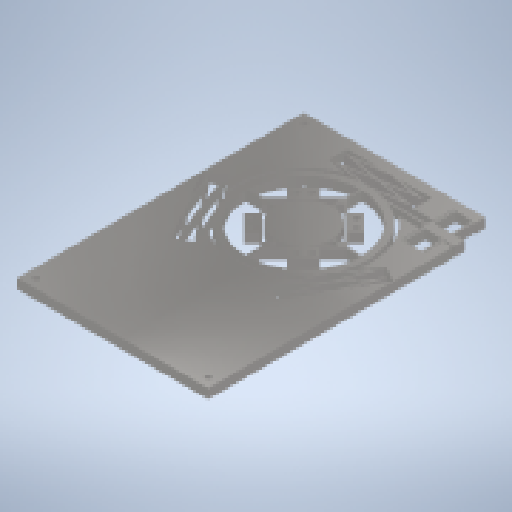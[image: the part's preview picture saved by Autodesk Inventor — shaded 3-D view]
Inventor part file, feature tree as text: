
AUTODESK INVENTOR PART (.ipt)
format: ipt  version: 2023 (Build 270158000, 158)  size: 652,288 bytes
history: native  units: mm
features: extrude x8, sketch x8, other x1
ambient origin geometry x8: Origin, YZ Plane, XZ Plane, XY Plane, X Axis, Y Axis, Z Axis, Center Point
bodies: Solid1 (feature_tree)
feature tree (17):
  other  "<userpath>\OneDrive\ClawdDrive\Objet3D\IminaProbe\Settings.xlsx"
  extrude  "Extrusion1"  Depth=100.0mm
  extrude  "Extrusion6"  TaperAngle=0.0deg  [1 undecoded]
  extrude  "Extrusion7"  Depth=1.0mm
  extrude  "Extrusion10"  Depth=1.0mm
  extrude  "Extrusion11"  Depth=50.0mm
  extrude  "Extrusion12"  Depth=30.0mm
  extrude  "Extrusion13"  Depth=67.082039mm
  extrude  "Extrusion14"  Depth=0.5mm
  sketch  "Sketch1"  dims[d0=150.0mm d1=100.0mm]
  sketch  "Sketch6"  dims[d2=5.0mm d3=0.0mm]
  sketch  "Sketch7"  dims[d14=1.0mm d16=1.0mm]
  sketch  "Sketch9"  dims[d19=1.0mm d23=52.849025mm d24=57.849025mm]
  sketch  "Sketch11"  dims[d25=67.849025mm]
  sketch  "Sketch12"  dims[d31=45.0deg d32=45.0deg d33=45.0deg d34=45.0deg d40=45.0deg d45=45.0deg d46=45.0deg d47=45.0deg d78=50.0mm]
  sketch  "Sketch13"  dims[d79=50.0mm d80=30.0mm]
  sketch  "Sketch14"  dims[d81=60.0mm d82=67.082039mm d83=0.5mm d84=0.5mm d91=72.082039mm d92=5.0mm d93=2.5mm d94=2.5mm d95=45.0deg d96=45.0deg d97=0.5mm d98=0.5mm d99=0.5mm d100=45.0deg d101=45.0deg d102=6.0mm d103=7.0mm d104=3.0mm d105=3.0mm d106=3.0mm d107=3.0mm d108=7.5mm d109=3.0mm d110=6.0mm d111=7.0mm d112=3.0mm d113=3.0mm d114=3.0mm d115=40.0mm d117=360.0deg d119=10.0mm d120=0.0mm d125=45.0deg d128=10.0mm d133=12.0mm d134=12.0mm d135=5.0mm d136=1.0mm d137=1.0mm d138=1.0mm d139=1.0mm d140=0.5mm d141=0.5mm d142=11.0mm d144=11.0mm d145=11.0mm d146=10.0mm d147=11.0mm d154=5.0mm d155=0.0mm d164=5.0mm d167=5.0mm d168=1.0mm d169=0.0mm d170=5.0mm d171=1.0mm d172=2.0mm d179=1.0mm d180=1.0mm d182=1.013794mm d183=20.0mm d185=6.013794mm d186=10.0mm d188=10.0mm d190=1.0mm d191=1.0mm d200=5.0mm d201=0.0mm d202=5.0mm d203=0.0mm d204=1.0mm d205=1.0mm d206=1.0mm d207=1.0mm d208=5.0mm d209=5.0mm d214=3.0mm d216=30.0mm d218=360.0deg d220=67.082039mm d221=5.0mm d222=0.0mm d223=5.0mm d224=0.0mm d225=5.0mm d226=0.0mm d227=5.0mm d228=5.0mm d229=5.0mm d230=5.0mm d231=5.0mm d232=5.0mm d233=3.0mm d234=3.0mm d235=3.0mm d236=5.0mm d237=0.0mm]
note: 1 required parameter value undecoded (feature->parameter linkage not recoverable at this tier; creation-order binding heuristic only, values carry confidence <= 0.55)
